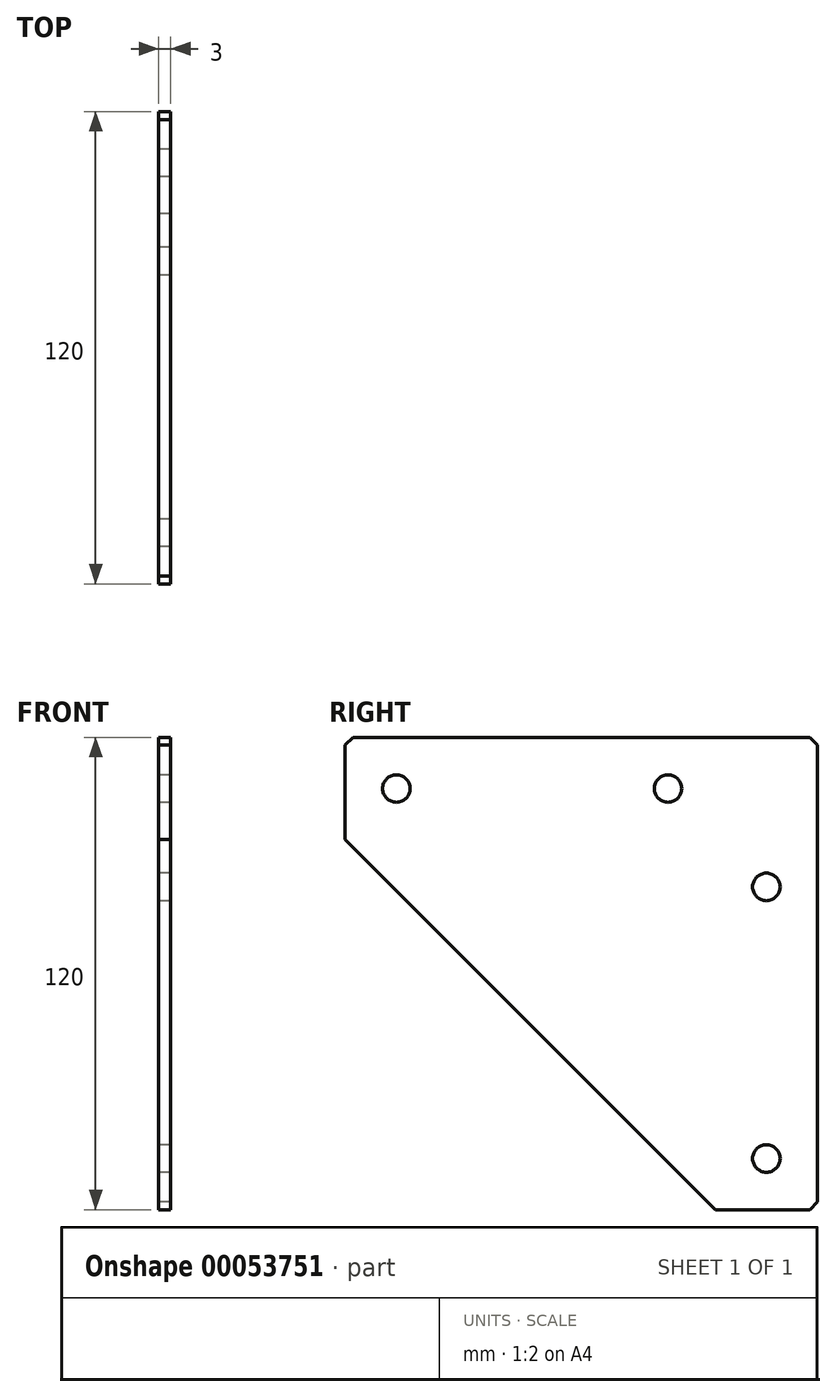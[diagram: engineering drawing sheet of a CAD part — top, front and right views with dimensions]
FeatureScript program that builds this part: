
annotation { "Feature Type Name" : "Feature", "Feature Type Description" : "" }
export const myFeature = defineFeature(function(context is Context, id is Id, definition is map)
    precondition{}
    {
        {
            var Q0;
            Q0=qCreatedBy(makeId("Right.planeOp"),FACE);
            var sketch = newSketch(context, id + "F0", { "sketchPlane" : qUnion([Q0])});
            skLineSegment(sketch, "E0", {"start": v(0, 0) * mm, "end": v(0, -120) * mm});
            skLineSegment(sketch, "E1", {"start": v(0, 0) * mm, "end": v(-120, 0) * mm});
            skLineSegment(sketch, "E2", {"start": v(0, -120) * mm, "end": v(-26, -120) * mm});
            skLineSegment(sketch, "E3", {"start": v(-120, 0) * mm, "end": v(-120, -26) * mm});
            skLineSegment(sketch, "E4", {"start": v(-26, -120) * mm, "end": v(-120, -26) * mm});
            skLineSegment(sketch, "E5", {"start": v(0, 0) * mm, "end": v(-73, -73) * mm});
            skCircle(sketch, "E6", {"center": v(-107, -13) * mm, "radius": 3.5 * mm});
            skCircle(sketch, "E7", {"center": v(-38, -13) * mm, "radius": 3.5 * mm});
            skCircle(sketch, "E8.MirrorC", {"center": v(-13, -38) * mm, "radius": 3.5 * mm});
            skCircle(sketch, "E9.MirrorC", {"center": v(-13, -107) * mm, "radius": 3.5 * mm});
            skSolve(sketch);
        }
        {
            var Q0;
            Q0 = qSketchRegion(id + "F0", true);
            extrude(context, id + "F1", {"entities" : qUnion([Q0]), "endBound" : BoundingType.SYMMETRIC, "depth" : 3 * mm});
        }
        {
            var Q0;
            Q0=makeQuery(id+"F1.opExtrude","SWEPT_EDGE",EDGE,{"disambiguationData":[OSD([sQuery(id+"F0.wireOp",EDGE,"E1"),sQuery(id+"F0.wireOp",EDGE,"E3")])]});
            var Q1;
            Q1=makeQuery(id+"F1.opExtrude","SWEPT_EDGE",EDGE,{"disambiguationData":[OSD([sQuery(id+"F0.wireOp",EDGE,"E0"),sQuery(id+"F0.wireOp",EDGE,"E1"),sQuery(id+"F0.wireOp",EDGE,"E5")])]});
            var Q2;
            Q2=makeQuery(id+"F1.opExtrude","SWEPT_EDGE",EDGE,{"disambiguationData":[OSD([sQuery(id+"F0.wireOp",EDGE,"E0"),sQuery(id+"F0.wireOp",EDGE,"E2")])]});
            chamfer(context, id + "F2", {"entities" : qUnion([Q0, Q1, Q2]), "width" : 2 * mm, "tangentPropagation" : true});
        }
    });
